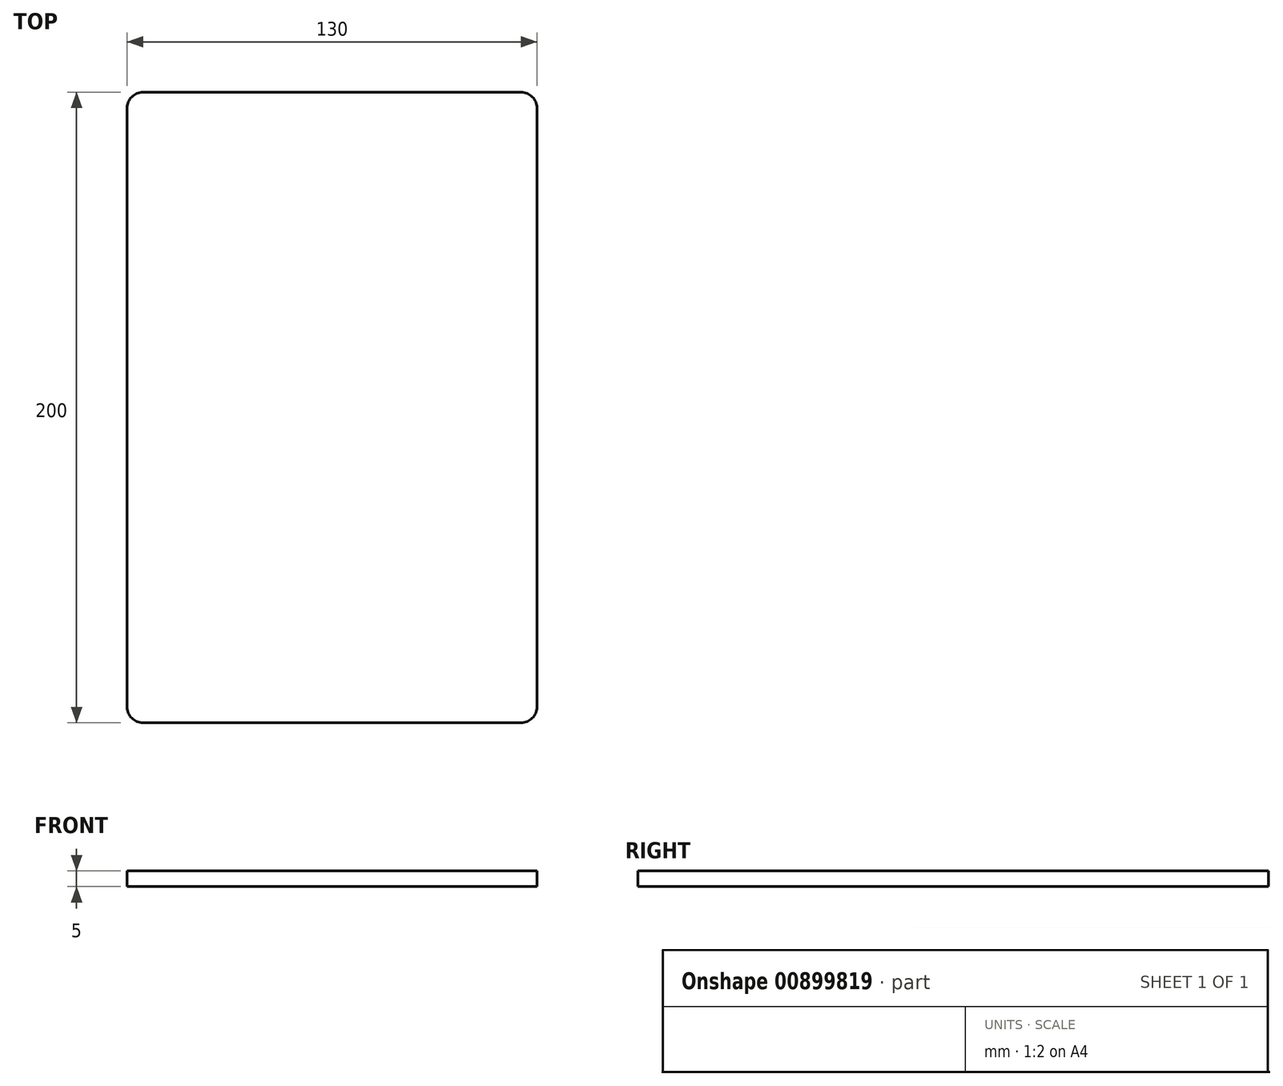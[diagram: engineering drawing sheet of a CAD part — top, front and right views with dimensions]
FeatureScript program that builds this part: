
annotation { "Feature Type Name" : "Feature", "Feature Type Description" : "" }
export const myFeature = defineFeature(function(context is Context, id is Id, definition is map)
    precondition{}
    {
        {
            var Q0;
            Q0=qCreatedBy(makeId("Top.planeOp"),FACE);
            var sketch = newSketch(context, id + "F0", { "sketchPlane" : qUnion([Q0])});
            skLineSegment(sketch, "E0.bottom", {"start": v(60, -100) * mm, "end": v(-60, -100) * mm});
            skLineSegment(sketch, "E0.top", {"start": v(60, 100) * mm, "end": v(-60, 100) * mm});
            skLineSegment(sketch, "E0.left", {"start": v(65, -95) * mm, "end": v(65, 95) * mm});
            skLineSegment(sketch, "E0.right", {"start": v(-65, -95) * mm, "end": v(-65, 95) * mm});
            skPoint(sketch, "E0.middle", {"position": v(0, 0) * mm});
            skPoint(sketch, "E1.visualSharp", {"position": v(-65, 100) * mm});
            skArc(sketch, "E1.filletArc", {"start": v(-60, 100) * mm, "mid": v(-63.54, 98.54) * mm, "end": v(-65, 95) * mm});
            skPoint(sketch, "E2.visualSharp", {"position": v(65, 100) * mm});
            skArc(sketch, "E2.filletArc", {"start": v(65, 95) * mm, "mid": v(63.54, 98.54) * mm, "end": v(60, 100) * mm});
            skPoint(sketch, "E3.visualSharp", {"position": v(65, -100) * mm});
            skArc(sketch, "E3.filletArc", {"start": v(60, -100) * mm, "mid": v(63.54, -98.54) * mm, "end": v(65, -95) * mm});
            skPoint(sketch, "E4.visualSharp", {"position": v(-65, -100) * mm});
            skArc(sketch, "E4.filletArc", {"start": v(-65, -95) * mm, "mid": v(-63.54, -98.54) * mm, "end": v(-60, -100) * mm});
            skSolve(sketch);
        }
        {
            var Q0;
            Q0=makeQuery(id+"F0.imprint","IMPRINT",FACE,{"disambiguationData":[TD([[makeQuery(id+"F0.imprint","IMPRINT",EDGE,{"derivedFrom":sQuery(id+"F0.wireOp",EDGE,"E0.bottom")}),-1.0]])]});
            extrude(context, id + "F1", {"entities" : qUnion([Q0]), "depth" : 5 * mm, "offsetDistance" : 25 * mm});
        }
    });
